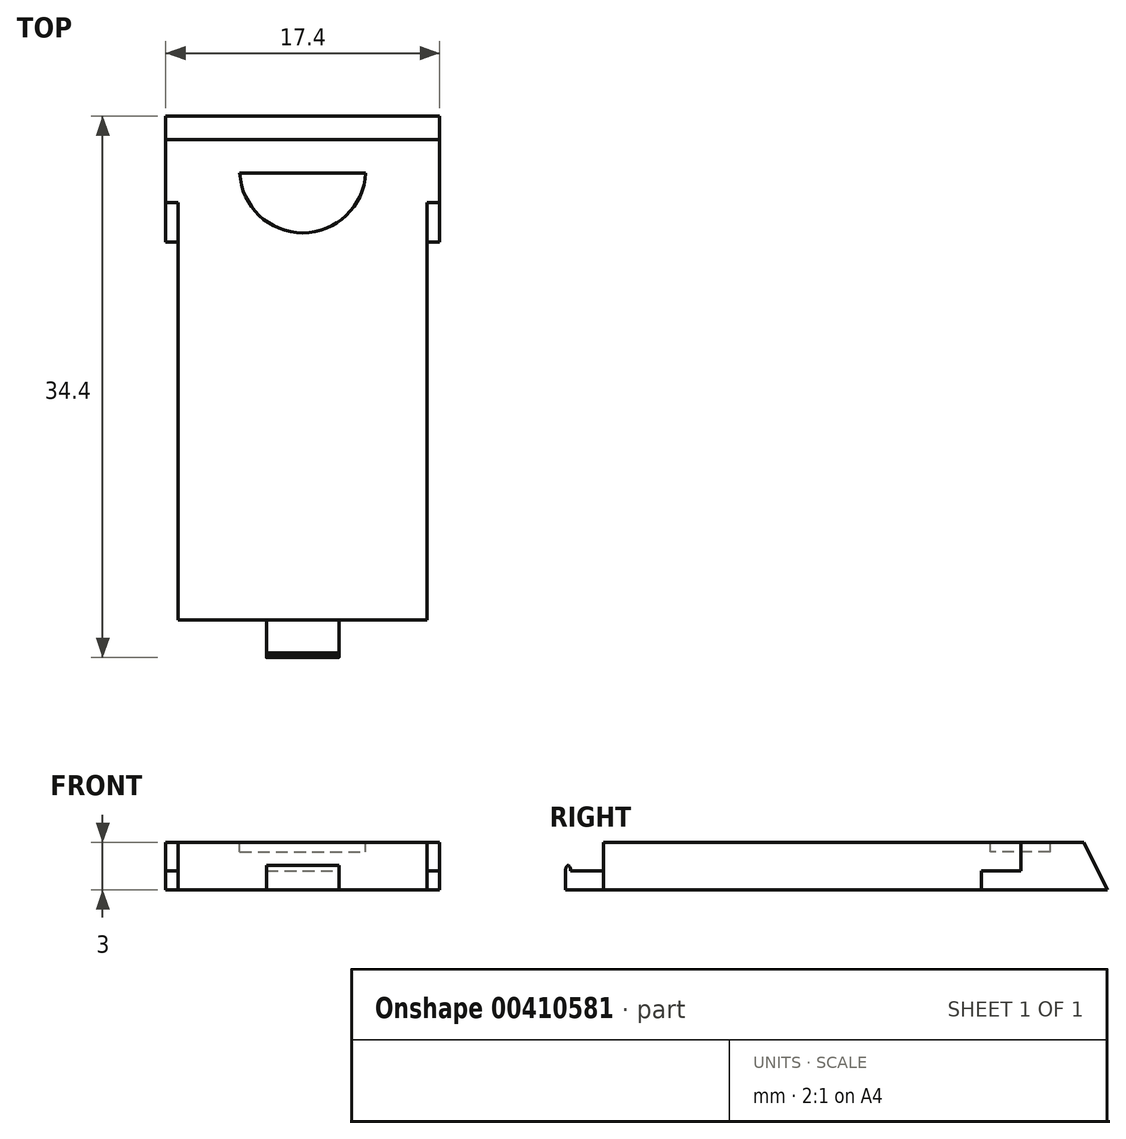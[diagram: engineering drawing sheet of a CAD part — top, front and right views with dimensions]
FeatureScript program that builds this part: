
annotation { "Feature Type Name" : "Feature", "Feature Type Description" : "" }
export const myFeature = defineFeature(function(context is Context, id is Id, definition is map)
    precondition{}
    {
        {
            var Q0;
            Q0=qCreatedBy(makeId("Top.planeOp"),FACE);
            var sketch = newSketch(context, id + "F0", { "sketchPlane" : qUnion([Q0])});
            skLineSegment(sketch, "E0.bottom", {"start": v(-7.9, 11) * mm, "end": v(7.9, 11) * mm});
            skLineSegment(sketch, "E0.top", {"start": v(-7.9, -21) * mm, "end": v(7.9, -21) * mm});
            skLineSegment(sketch, "E0.left", {"start": v(-7.9, 11) * mm, "end": v(-7.9, -21) * mm});
            skLineSegment(sketch, "E0.right", {"start": v(7.9, 11) * mm, "end": v(7.9, -21) * mm});
            skSolve(sketch);
        }
        {
            var Q0;
            Q0 = qSketchRegion(id + "F0", true);
            var Q1;
            Q1=makeQuery(id+"F0.imprint","IMPRINT",FACE,{"disambiguationData":[TD([[makeQuery(id+"F0.imprint","IMPRINT",EDGE,{"derivedFrom":sQuery(id+"F0.wireOp",EDGE,"E0.bottom")}),-1.0]])]});
            extrude(context, id + "F1", {"entities" : qUnion([Q0, Q1]), "depth" : 3 * mm});
        }
        {
            var Q0;
            Q0=makeQuery(id+"F1.opExtrude","SWEPT_FACE",FACE,{"disambiguationData":[OSD([sQuery(id+"F0.wireOp",EDGE,"E0.right")])]});
            var sketch = newSketch(context, id + "F2", { "sketchPlane" : qUnion([Q0])});
            skLineSegment(sketch, "E1.0", {"start": v(11, 3) * mm, "end": v(-21, 3) * mm});
            skLineSegment(sketch, "E2.0", {"start": v(11, 3) * mm, "end": v(11, 0) * mm});
            skLineSegment(sketch, "E3.0", {"start": v(11, 0) * mm, "end": v(-21, 0) * mm});
            skLineSegment(sketch, "E4.0", {"start": v(-21, 3) * mm, "end": v(-21, 0) * mm});
            skLineSegment(sketch, "E5.0", {"start": v(3, 1.2) * mm, "end": v(3, 0) * mm});
            skLineSegment(sketch, "E6.0", {"start": v(5.5, 3) * mm, "end": v(5.5, 1.2) * mm});
            skLineSegment(sketch, "E7.0", {"start": v(5.5, 1.2) * mm, "end": v(3, 1.2) * mm});
            skSolve(sketch);
        }
        {
            var Q0;
            {var subQ2=sQuery(id+"F2.wireOp",EDGE,"E2.0");Q0=makeQuery(id+"F2.imprint","IMPRINT",FACE,{"disambiguationData":[TD([[makeQuery(id+"F2.imprint","IMPRINT",EDGE,{"derivedFrom":subQ2}),-1.0]])]});}
            extrude(context, id + "F3", {"entities" : qUnion([Q0]), "depth" : 0.8 * mm});
        }
        {
            var Q0;
            Q0=makeQuery(id+"F3.opExtrude","SWEPT_BODY",BODY,{"disambiguationData":[OSD([sQuery(id+"F2.wireOp",EDGE,"E1.0"),sQuery(id+"F2.wireOp",EDGE,"E2.0"),sQuery(id+"F2.wireOp",EDGE,"E3.0"),sQuery(id+"F2.wireOp",EDGE,"E5.0"),sQuery(id+"F2.wireOp",EDGE,"E6.0"),sQuery(id+"F2.wireOp",EDGE,"E7.0")])]});
            var Q1;
            Q1=qCreatedBy(makeId("Right.planeOp"),FACE);
            mirror(context, id + "F4", {"operationType" : NewBodyOperationType.ADD, "entities" : qUnion([Q0]), "mirrorPlane" : qUnion([Q1])});
        }
        {
            var Q0;
            Q0=makeQuery(id+"F1.opExtrude","SWEPT_FACE",FACE,{"disambiguationData":[OSD([sQuery(id+"F0.wireOp",EDGE,"E0.top")])]});
            var sketch = newSketch(context, id + "F5", { "sketchPlane" : qUnion([Q0])});
            skLineSegment(sketch, "E8.0", {"start": v(-7.9, 0) * mm, "end": v(7.9, 0) * mm});
            skLineSegment(sketch, "E9.0", {"start": v(-7.9, 3) * mm, "end": v(7.9, 3) * mm});
            skLineSegment(sketch, "E10", {"start": v(0, 3) * mm, "end": v(0, 0) * mm, "construction": true});
            skLineSegment(sketch, "E11.0", {"start": v(-7.9, 1.2) * mm, "end": v(7.9, 1.2) * mm});
            skLineSegment(sketch, "E12", {"start": v(-2.3, 1.2) * mm, "end": v(-2.3, 0) * mm});
            skLineSegment(sketch, "E13", {"start": v(2.3, 1.2) * mm, "end": v(2.3, 0) * mm});
            skSolve(sketch);
        }
        {
            var Q0;
            Q0 = qSketchRegion(id + "F5", true);
            extrude(context, id + "F6", {"entities" : qUnion([Q0]), "operationType" : NewBodyOperationType.ADD, "depth" : 2.4 * mm});
        }
        {
            var Q0;
            {var subQ0=makeQuery(id+"F3.opExtrude","SWEPT_FACE",FACE,{"disambiguationData":[OSD([sQuery(id+"F2.wireOp",EDGE,"E1.0")])]});Q0=makeQuery(id+"F4.boolean.opBoolean","MERGE",FACE,{"derivedFrom":[makeQuery(id+"F1.opExtrude","CAP_FACE",FACE,{"disambiguationData":[OSD([sQuery(id+"F0.wireOp",EDGE,"E0.bottom"),sQuery(id+"F0.wireOp",EDGE,"E0.top"),sQuery(id+"F0.wireOp",EDGE,"E0.left"),sQuery(id+"F0.wireOp",EDGE,"E0.right")])],"isStart":false}),subQ0,makeQuery(id+"F4.opPattern","COPY",FACE,{"derivedFrom":subQ0,"instanceName":"1"})]});}
            var sketch = newSketch(context, id + "F7", { "sketchPlane" : qUnion([Q0])});
            skLineSegment(sketch, "E14.0", {"start": v(-8.7, 11) * mm, "end": v(8.7, 11) * mm, "construction": true});
            skLineSegment(sketch, "E15.0", {"start": v(-7.9, -21) * mm, "end": v(7.9, -21) * mm, "construction": true});
            skLineSegment(sketch, "E16", {"start": v(0, 11) * mm, "end": v(0, -21) * mm, "construction": true});
            skLineSegment(sketch, "E17", {"start": v(-4, 7.38) * mm, "end": v(4, 7.38) * mm});
            skArc(sketch, "E18", {"start": v(-4, 7.38) * mm, "mid": v(0, 3.58) * mm, "end": v(4, 7.38) * mm});
            skSolve(sketch);
        }
        {
            var Q0;
            Q0 = qSketchRegion(id + "F7", true);
            extrude(context, id + "F8", {"entities" : qUnion([Q0]), "operationType" : NewBodyOperationType.REMOVE, "oppositeDirection" : true, "depth" : 0.6 * mm});
        }
        {
            var Q0;
            Q0=makeQuery(id+"F6.opExtrude","SWEPT_FACE",FACE,{"disambiguationData":[OSD([sQuery(id+"F5.wireOp",EDGE,"E11.0")])]});
            var sketch = newSketch(context, id + "F9", { "sketchPlane" : qUnion([Q0])});
            skLineSegment(sketch, "E19.0", {"start": v(-2.3, -23.4) * mm, "end": v(2.3, -23.4) * mm});
            skLineSegment(sketch, "E20.0", {"start": v(-2.3, -23.1) * mm, "end": v(2.3, -23.1) * mm});
            skLineSegment(sketch, "E21", {"start": v(-2.3, -23.4) * mm, "end": v(-2.3, -23.1) * mm});
            skLineSegment(sketch, "E22", {"start": v(2.3, -23.4) * mm, "end": v(2.3, -23.1) * mm});
            skSolve(sketch);
        }
        {
            var Q0;
            Q0 = qSketchRegion(id + "F9", true);
            extrude(context, id + "F10", {"entities" : qUnion([Q0]), "operationType" : NewBodyOperationType.ADD, "depth" : 0.4 * mm});
        }
        {
            var Q0;
            Q0=makeQuery(id+"F10.opExtrude","CAP_EDGE",EDGE,{"disambiguationData":[OSD([sQuery(id+"F9.wireOp",EDGE,"E19.0")])],"isStart":false});
            var Q1;
            Q1=makeQuery(id+"F10.opExtrude","CAP_EDGE",EDGE,{"disambiguationData":[OSD([sQuery(id+"F9.wireOp",EDGE,"E20.0")])],"isStart":false});
            fillet(context, id + "F11", {"entities" : qUnion([Q0, Q1]), "radius" : 0.3 * mm, "tangentPropagation" : true, "allowEdgeOverflow" : false});
        }
        {
            var Q0;
            {var subQ0=makeQuery(id+"F3.opExtrude","SWEPT_EDGE",EDGE,{"disambiguationData":[OSD([sQuery(id+"F2.wireOp",EDGE,"E1.0"),sQuery(id+"F2.wireOp",EDGE,"E2.0")])]});Q0=makeQuery(id+"F4.boolean.opBoolean","MERGE",EDGE,{"derivedFrom":[makeQuery(id+"F1.opExtrude","CAP_EDGE",EDGE,{"disambiguationData":[OSD([sQuery(id+"F0.wireOp",EDGE,"E0.bottom")])],"isStart":false}),subQ0,makeQuery(id+"F4.opPattern","COPY",EDGE,{"derivedFrom":subQ0,"instanceName":"1"})]});}
            chamfer(context, id + "F12", {"entities" : qUnion([Q0]), "chamferType" : ChamferType.TWO_OFFSETS, "width1" : 3 * mm, "oppositeDirection" : false, "width2" : 1.5 * mm, "tangentPropagation" : true});
        }
    });
